# Revit family: Table-Teknion-CWRCH-Height_Adjustable_Reception_Classic_Desk-R2022
name_source: partatom
category: Furniture
units: mm (PartAtom-declared; Revit-internal decimal feet)

## family parameters
Always vertical = Yes
Cut with Voids When Loaded = No
OmniClass Number = 23.40.20.00
OmniClass Title = General Furniture and Specialties
Render Appearance Source = Family Geometry
Room Calculation Point = No
Shared = Yes
Work Plane-Based = No

## types (2) — shared parameters
Assembly Code = E2020200
Depth = 37 "
Left = Yes
Manufacturer = Teknion
Manufacturer Fax = 416.661.4586
Part Number = CWRCH
Product Documentation Link = https://assets.teknion.com
Product Line = Reception
Product Page URL = https://www.teknion.com
Series = Custom Wood
Sustainability Data = https://www.teknion.com
URL = www.teknion.com
Unit Weight URL = http://www.teknion.com
Warranty = http://www.teknion.com
zero-valued in all types: Default Elevation

## per-type parameters (varying)
| type | Description | LB | LF | Model |
| Box/Box/File Storage | Teknion Reception, H/A Classic Desk, 36" Depth, Left, Box/Box/File Storage | Yes | No | CWRCH36_B |
| File/File Storage | Teknion Reception, H/A Classic Desk, 36" Depth, Left, File/File Storage | No | Yes | CWRCH36_F |

## geometry (parser evidence)
native form markers: Sweep x3
no freeform markers — native parametric forms only
